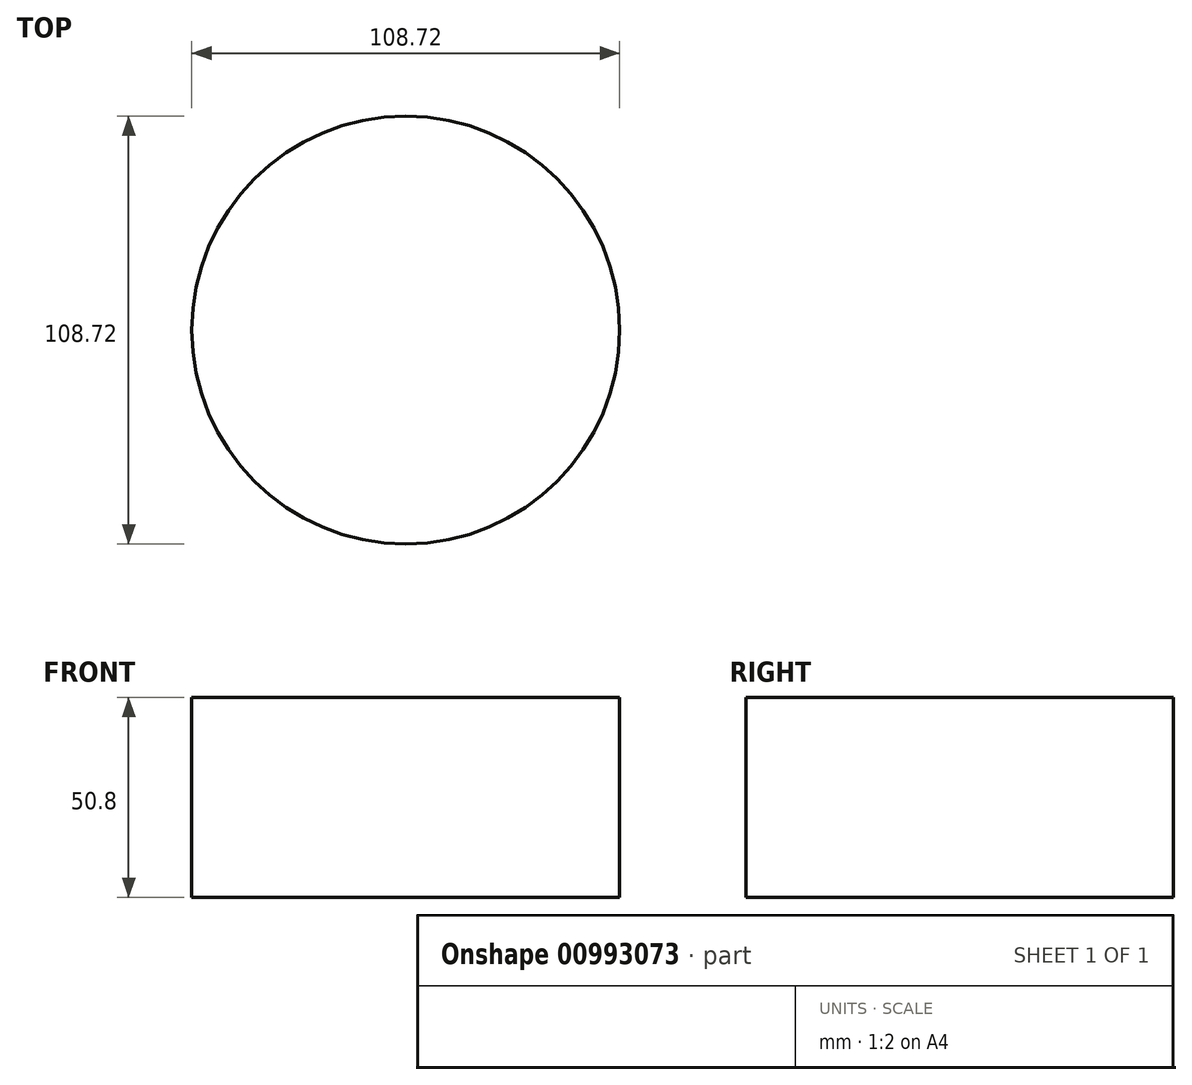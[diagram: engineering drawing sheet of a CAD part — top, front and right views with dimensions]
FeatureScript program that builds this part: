
annotation { "Feature Type Name" : "Feature", "Feature Type Description" : "" }
export const myFeature = defineFeature(function(context is Context, id is Id, definition is map)
    precondition{}
    {
        {
            var Q0;
            Q0=qCreatedBy(makeId("Top.planeOp"),FACE);
            var sketch = newSketch(context, id + "F0", { "sketchPlane" : qUnion([Q0])});
            skCircle(sketch, "E0", {"center": v(0, 0) * mm, "radius": 54.36 * mm});
            skSolve(sketch);
        }
        {
            var Q0;
            Q0 = qSketchRegion(id + "F0", true);
            extrude(context, id + "F1", {"entities" : qUnion([Q0]), "depth" : 50.8 * mm, "offsetDistance" : 25.4 * mm});
        }
    });
